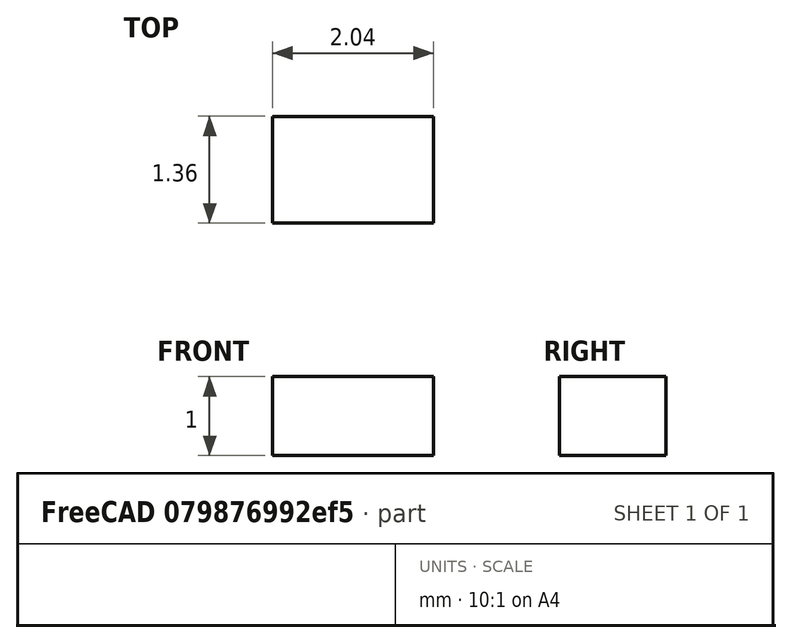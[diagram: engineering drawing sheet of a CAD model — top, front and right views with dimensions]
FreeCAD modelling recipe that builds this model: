
FCSTD DOCUMENT  (FreeCAD 0.18R15969 (Git))
Label: Capacitor 100n
License: All rights reserved
LicenseURL: http://en.wikipedia.org/wiki/All_rights_reserved
objects: Sketcher::SketchObject×1, PartDesign::Pad×1, PartDesign::Body×1
note: 4 computed .brp shape members not serialized (recipe doc carries the construction recipe); baked Part::Feature solids carry a one-line shape summary decoded from their .brp

FEATURE [Sketcher::SketchObject] Sketch
  MapMode = 5
  Support = -> [XY_Plane]
  expr: Constraints[16] = 1.95 + 0.1
  expr: Constraints[17] = 1.25 + 0.1
  sketch-geometry (7):
    g0: LineSegment StartX=-1.025 StartY=-0.675 StartZ=0 EndX=1.025 EndY=-0.675 EndZ=0
    g1: LineSegment StartX=1.025 StartY=-0.675 StartZ=0 EndX=1.025 EndY=0.675 EndZ=0
    g2: LineSegment StartX=1.025 StartY=0.675 StartZ=0 EndX=-1.025 EndY=0.675 EndZ=0
    g3: LineSegment StartX=-1.025 StartY=0.675 StartZ=0 EndX=-1.025 EndY=-0.675 EndZ=0
    g4: LineSegment [constr] StartX=-1.025 StartY=0.675 StartZ=0 EndX=0 EndY=0 EndZ=0
    g5: LineSegment [constr] StartX=0 StartY=0 StartZ=0 EndX=1.025 EndY=0.675 EndZ=0
    g6: LineSegment [constr] StartX=0 StartY=0 StartZ=0 EndX=-1.025 EndY=-0.675 EndZ=0
  constraints (18):
    c: Coincident(g0,g1)
    c: Coincident(g1,g2)
    c: Coincident(g2,g3)
    c: Coincident(g3,g0)
    c: Horizontal(g0)
    c: Horizontal(g2)
    c: Vertical(g1)
    c: Vertical(g3)
    c: Coincident(g4,g2)
    c: Coincident(g4,g-1)
    c: Coincident(g5,g-1)
    c: Coincident(g5,g1)
    c: Coincident(g6,g-1)
    c: Coincident(g6,g0)
    c: Equal(g5,g4)
    c: Equal(g4,g6)
    c: DistanceX(g2,g2) = 2.05
    c: DistanceY(g3,g3) = 1.35
FEATURE [PartDesign::Pad] Pad
  Length = 1
  Length2 = 100
  Profile = -> Sketch
  Refine = true
  Type = 0
  expr: Length = 0.9mm + 0.1mm
FEATURE [PartDesign::Body] Body  label="Capacitor 100n"
  Group = -> [Sketch,Pad]
  Origin = -> Origin
  Tip = -> Pad
